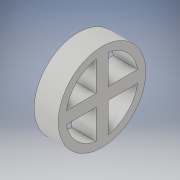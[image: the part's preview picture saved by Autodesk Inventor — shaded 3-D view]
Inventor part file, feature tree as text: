
AUTODESK INVENTOR PART (.ipt)
format: ipt  version: 2018 (Build 220112000, 112)  size: 115,712 bytes
history: native  units: in
note: dims shown in document units (in); Inventor stores cm internally (conversion verified against a paired STEP export)
features: extrude x1, sketch x1
ambient origin geometry x8: Origin, YZ Plane, XZ Plane, XY Plane, X Axis, Y Axis, Z Axis, Center Point
bodies: Solid1 (feature_tree)
feature tree (2):
  extrude  "Extrusion1"  Depth=0.25in
  sketch  "Sketch1"  dims[d0=0.91in d4=0.75in d5=0.25in d6=0.0in]
